# Revit family: Fixture_Wall_Bracket-American_Standard-8888.036
name_source: partatom
category: Specialty Equipment
revit_build: Autodesk Revit 2014 (Build: 20130308_1515(x64)
units: mm (PartAtom-declared; Revit-internal decimal feet)

## types (1)
- 8888.036
    Assembly Code = C1030200
    Default Elevation = 56"
    Description = Fixture Wall Bracket
    Finish = Brass-American Standard-002-Polished Chrome
    Installation Type = Wall Mounted
    Length = 2 3/16"
    Manufacturer = American Standard
    Material = Brass-American Standard-002-Polished Chrome
    Model = 8888.036
    Price = Prices may vary. Please consult Manufacturer Representative for most up-to-date price list.
    Product Documentation Link = https://www.americanstandard-us.com
    Product Page URL = https://www.americanstandard-us.com
    URL = https://www.americanstandard-us.com
    Warranty Information = One Year Limited Warranty
    Width = 1 1/2"

## geometry (parser evidence)
native form markers: Sweep x3
no freeform markers — native parametric forms only
